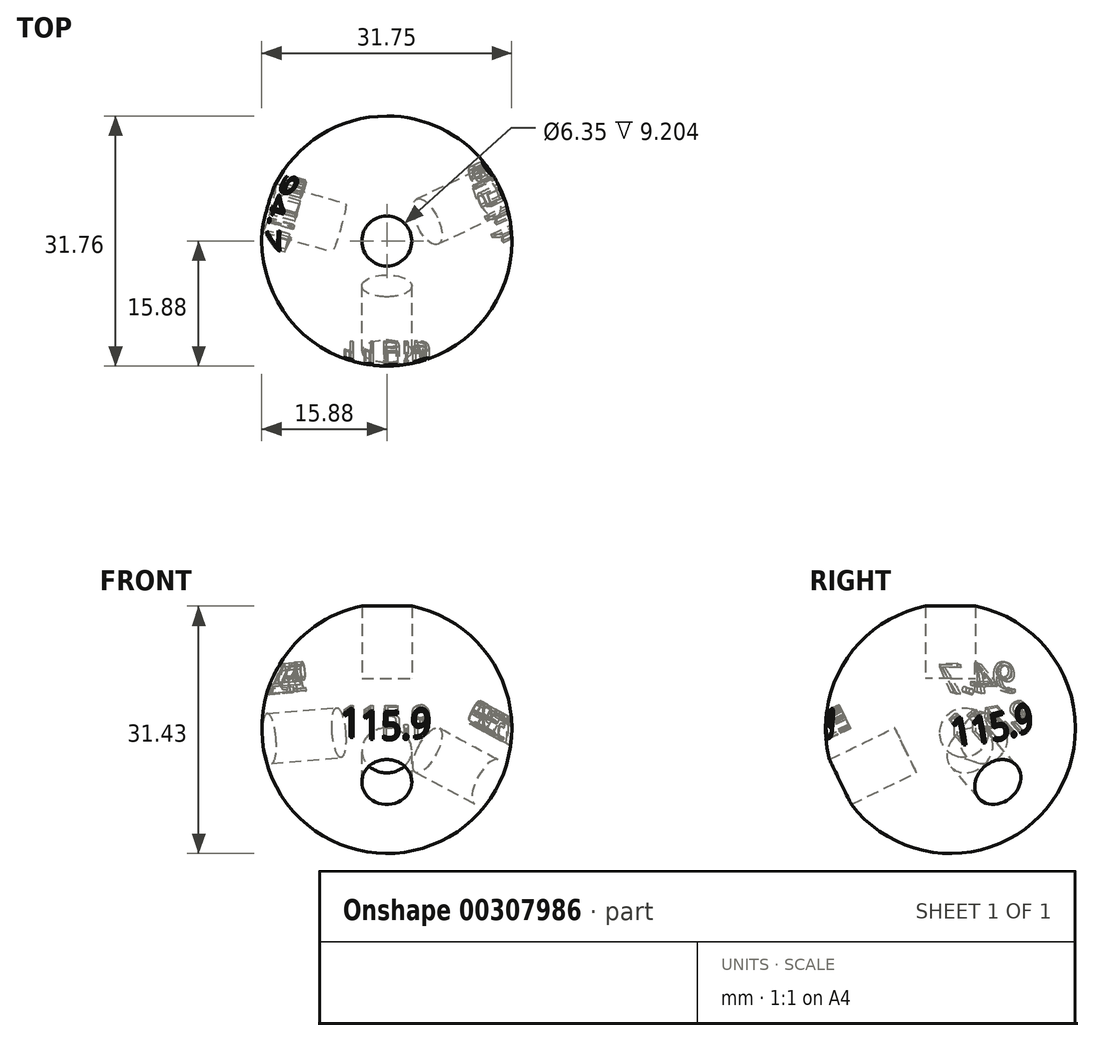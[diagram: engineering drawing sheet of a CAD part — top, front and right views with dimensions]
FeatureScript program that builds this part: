
annotation { "Feature Type Name" : "Feature", "Feature Type Description" : "" }
export const myFeature = defineFeature(function(context is Context, id is Id, definition is map)
    precondition{}
    {
        {
            var Q0;
            Q0=qCreatedBy(makeId("Front.planeOp"),FACE);
            var sketch = newSketch(context, id + "F0", { "sketchPlane" : qUnion([Q0])});
            skCircle(sketch, "E0", {"center": v(0, 0) * mm, "radius": 15.88 * mm});
            skLineSegment(sketch, "E1", {"start": v(0, 0) * mm, "end": v(50.88, 0) * mm, "construction": true});
            skLineSegment(sketch, "E2", {"start": v(50.88, 0) * mm, "end": v(0, 0) * mm, "construction": true});
            skLineSegment(sketch, "E3", {"start": v(0, 55.5) * mm, "end": v(0, 0) * mm, "construction": true});
            skSolve(sketch);
        }
        {
            var Q0;
            Q0=qCreatedBy(makeId("Top.planeOp"),FACE);
            var sketch = newSketch(context, id + "F1", { "sketchPlane" : qUnion([Q0])});
            skArc(sketch, "E4", {"start": v(0, 15.88) * mm, "mid": v(-15.88, 0) * mm, "end": v(0, -15.88) * mm});
            skLineSegment(sketch, "E5", {"start": v(0, 15.88) * mm, "end": v(0, -15.88) * mm});
            skLineSegment(sketch, "E6", {"start": v(0, 0) * mm, "end": v(0, 50.33) * mm, "construction": true});
            skSolve(sketch);
        }
        {
            var Q0;
            Q0 = qSketchRegion(id + "F1", true);
            var Q1;
            Q1=sQuery(id+"F0.wireOp",EDGE,"E0");
            revolve(context, id + "F2", {"entities" : qUnion([Q0]), "axis" : qUnion([Q1]), "revolveType" : RevolveType.FULL});
        }
        {
            var Q0;
            Q0=qCreatedBy(makeId("Top.planeOp"),FACE);
            cPlane(context, id + "F3", {"entities" : qUnion([Q0]), "cplaneType" : CPlaneType.OFFSET, "offset" : 6.35 * mm, "width" : 152.4 * mm, "height" : 152.4 * mm});
        }
        {
            var Q0;
            Q0=qCreatedBy(id+"F3.planeOp",FACE);
            var sketch = newSketch(context, id + "F4", { "sketchPlane" : qUnion([Q0])});
            skCircle(sketch, "E7", {"center": v(0, 0) * mm, "radius": 3.18 * mm});
            skSolve(sketch);
        }
        {
            var Q0;
            Q0 = qSketchRegion(id + "F4", true);
            extrude(context, id + "F5", {"entities" : qUnion([Q0]), "depth" : 25.4 * mm});
        }
        {
            var Q0;
            Q0=qCreatedBy(makeId("Top.planeOp"),FACE);
            var sketch = newSketch(context, id + "F6", { "sketchPlane" : qUnion([Q0])});
            skLineSegment(sketch, "E8", {"start": v(0, 0) * mm, "end": v(53.65, 0) * mm, "construction": true});
            skLineSegment(sketch, "E9", {"start": v(0, 0) * mm, "end": v(0, 59) * mm, "construction": true});
            skSolve(sketch);
        }
        {
            var Q0;
            Q0=qCreatedBy(makeId("Front.planeOp"),FACE);
            var sketch = newSketch(context, id + "F7", { "sketchPlane" : qUnion([Q0])});
            skLineSegment(sketch, "E10", {"start": v(0, 0) * mm, "end": v(0, 58.8) * mm, "construction": true});
            skSolve(sketch);
        }
        {
            var Q0;
            Q0=makeQuery(id+"F5.opExtrude","SWEPT_BODY",BODY,{"disambiguationData":[OSD([sQuery(id+"F4.wireOp",EDGE,"E7")])]});
            var Q1;
            Q1=sQuery(id+"F6.wireOp",EDGE,"E8");
            transform(context, id + "F8", {"entities" : qUnion([Q0]), "transformType" : TransformType.ROTATION, "transformAxis" : qUnion([Q1]), "angle" : 115.9 * degree, "makeCopy" : true});
        }
        {
            var Q0;
            Q0=makeQuery(id+"F8.opPattern","COPY",FACE,{"derivedFrom":makeQuery(id+"F5.opExtrude","CAP_FACE",FACE,{"disambiguationData":[OSD([sQuery(id+"F4.wireOp",EDGE,"E7")])],"isStart":false}),"instanceName":"1"});
            cPlane(context, id + "F9", {"entities" : qUnion([Q0]), "cplaneType" : CPlaneType.OFFSET, "offset" : 12.7 * mm, "oppositeDirection" : true, "width" : 152.4 * mm, "height" : 152.4 * mm});
        }
        {
            var Q0;
            Q0=qCreatedBy(id+"F9.planeOp",FACE);
            var sketch = newSketch(context, id + "F10", { "sketchPlane" : qUnion([Q0])});
            skText(sketch, "E11", { "text": "115.9", "fontName": "OpenSans-Regular.ttf"});
            const initialGuessF10  = {"E11": [-0.00586, 0.00563, 1, 0, 0.00323]};
            skSetInitialGuess(sketch, initialGuessF10);
            skSolve(sketch);
        }
        {
            var Q0;
            Q0 = qSketchRegion(id + "F10", true);
            extrude(context, id + "F11", {"entities" : qUnion([Q0]), "operationType" : NewBodyOperationType.REMOVE, "oppositeDirection" : true, "depth" : 7.62 * mm});
        }
        {
            var Q0;
            Q0=makeQuery(id+"F8.opPattern","COPY",BODY,{"derivedFrom":makeQuery(id+"F5.opExtrude","SWEPT_BODY",BODY,{"disambiguationData":[OSD([sQuery(id+"F4.wireOp",EDGE,"E7")])]}),"instanceName":"1"});
            var Q1;
            Q1=sQuery(id+"F7.wireOp",EDGE,"E10");
            transform(context, id + "F12", {"entities" : qUnion([Q0]), "transformType" : TransformType.ROTATION, "transformAxis" : qUnion([Q1]), "angle" : 115.4 * degree, "makeCopy" : true});
        }
        {
            var Q0;
            Q0=makeQuery(id+"F12.opPattern","COPY",FACE,{"derivedFrom":makeQuery(id+"F8.opPattern","COPY",FACE,{"derivedFrom":makeQuery(id+"F5.opExtrude","CAP_FACE",FACE,{"disambiguationData":[OSD([sQuery(id+"F4.wireOp",EDGE,"E7")])],"isStart":false}),"instanceName":"1"}),"instanceName":"1"});
            cPlane(context, id + "F13", {"entities" : qUnion([Q0]), "cplaneType" : CPlaneType.OFFSET, "offset" : 12.7 * mm, "oppositeDirection" : true, "width" : 152.4 * mm, "height" : 152.4 * mm});
        }
        {
            var Q0;
            Q0=qCreatedBy(id+"F13.planeOp",FACE);
            var sketch = newSketch(context, id + "F14", { "sketchPlane" : qUnion([Q0])});
            skText(sketch, "E12", { "text": "115.9", "fontName": "OpenSans-Regular.ttf"});
            const initialGuessF14  = {"E12": [-0.0054, 0.00557, 1, 0, 0.00314]};
            skSetInitialGuess(sketch, initialGuessF14);
            skSolve(sketch);
        }
        {
            var Q0;
            Q0 = qSketchRegion(id + "F14", true);
            extrude(context, id + "F15", {"entities" : qUnion([Q0]), "operationType" : NewBodyOperationType.REMOVE, "oppositeDirection" : true, "depth" : 7.62 * mm});
        }
        {
            var Q0;
            Q0=qCreatedBy(makeId("Front.planeOp"),FACE);
            var sketch = newSketch(context, id + "F16", { "sketchPlane" : qUnion([Q0])});
            skLineSegment(sketch, "E13", {"start": v(0, 0) * mm, "end": v(62.5, 0) * mm, "construction": true});
            skLineSegment(sketch, "E14", {"start": v(0, 0) * mm, "end": v(0, 62.68) * mm, "construction": true});
            skSolve(sketch);
        }
        {
            var Q0;
            Q0=makeQuery(id+"F5.opExtrude","SWEPT_BODY",BODY,{"disambiguationData":[OSD([sQuery(id+"F4.wireOp",EDGE,"E7")])]});
            var Q1;
            Q1=sQuery(id+"F16.wireOp",EDGE,"E13");
            transform(context, id + "F17", {"entities" : qUnion([Q0]), "transformType" : TransformType.ROTATION, "transformAxis" : qUnion([Q1]), "angle" : 94.7 * degree, "makeCopy" : true});
        }
        {
            var Q0;
            Q0=qCreatedBy(makeId("Front.planeOp"),FACE);
            var sketch = newSketch(context, id + "F18", { "sketchPlane" : qUnion([Q0])});
            skLineSegment(sketch, "E15", {"start": v(0, 0) * mm, "end": v(0, 64.7) * mm, "construction": true});
            skSolve(sketch);
        }
        {
            var Q0;
            Q0=makeQuery(id+"F17.opPattern","COPY",BODY,{"derivedFrom":makeQuery(id+"F5.opExtrude","SWEPT_BODY",BODY,{"disambiguationData":[OSD([sQuery(id+"F4.wireOp",EDGE,"E7")])]}),"instanceName":"1"});
            var Q1;
            Q1=sQuery(id+"F18.wireOp",EDGE,"E15");
            transform(context, id + "F19", {"entities" : qUnion([Q0]), "transformType" : TransformType.ROTATION, "transformAxis" : qUnion([Q1]), "angle" : 105.7 * degree, "oppositeDirection" : true, "makeCopy" : false});
        }
        {
            var Q0;
            Q0=makeQuery(id+"F17.opPattern","COPY",FACE,{"derivedFrom":makeQuery(id+"F5.opExtrude","CAP_FACE",FACE,{"disambiguationData":[OSD([sQuery(id+"F4.wireOp",EDGE,"E7")])],"isStart":false}),"instanceName":"1"});
            cPlane(context, id + "F20", {"entities" : qUnion([Q0]), "cplaneType" : CPlaneType.OFFSET, "offset" : 12.7 * mm, "oppositeDirection" : true, "width" : 152.4 * mm, "height" : 152.4 * mm});
        }
        {
            var Q0;
            Q0=qCreatedBy(id+"F20.planeOp",FACE);
            var sketch = newSketch(context, id + "F21", { "sketchPlane" : qUnion([Q0])});
            skText(sketch, "E16", { "text": "94.7", "fontName": "OpenSans-Regular.ttf"});
            const initialGuessF21  = {"E16": [-0.00508, 0.00568, 1, 0, 0.00364]};
            skSetInitialGuess(sketch, initialGuessF21);
            skSolve(sketch);
        }
        {
            var Q0;
            Q0 = qSketchRegion(id + "F21", true);
            extrude(context, id + "F22", {"entities" : qUnion([Q0]), "operationType" : NewBodyOperationType.REMOVE, "oppositeDirection" : true, "depth" : 7.62 * mm});
        }
        {
            var Q0;
            Q0=makeQuery(id+"F5.opExtrude","SWEPT_BODY",BODY,{"disambiguationData":[OSD([sQuery(id+"F4.wireOp",EDGE,"E7")])]});
            var Q1;
            Q1=makeQuery(id+"F17.opPattern","COPY",BODY,{"derivedFrom":makeQuery(id+"F5.opExtrude","SWEPT_BODY",BODY,{"disambiguationData":[OSD([sQuery(id+"F4.wireOp",EDGE,"E7")])]}),"instanceName":"1"});
            var Q2;
            Q2=makeQuery(id+"F8.opPattern","COPY",BODY,{"derivedFrom":makeQuery(id+"F5.opExtrude","SWEPT_BODY",BODY,{"disambiguationData":[OSD([sQuery(id+"F4.wireOp",EDGE,"E7")])]}),"instanceName":"1"});
            var Q3;
            Q3=makeQuery(id+"F12.opPattern","COPY",BODY,{"derivedFrom":makeQuery(id+"F8.opPattern","COPY",BODY,{"derivedFrom":makeQuery(id+"F5.opExtrude","SWEPT_BODY",BODY,{"disambiguationData":[OSD([sQuery(id+"F4.wireOp",EDGE,"E7")])]}),"instanceName":"1"}),"instanceName":"1"});
            var Q4;
            Q4=makeQuery(id+"F2.opRevolve","SWEPT_BODY",BODY,{"disambiguationData":[OSD([sQuery(id+"F1.wireOp",EDGE,"E4"),sQuery(id+"F1.wireOp",EDGE,"E5")])]});
            booleanBodies(context, id + "F23", {"operationType" : BooleanOperationType.SUBTRACTION, "tools" : qUnion([Q0, Q1, Q2, Q3]), "targets" : qUnion([Q4])});
        }
    });
